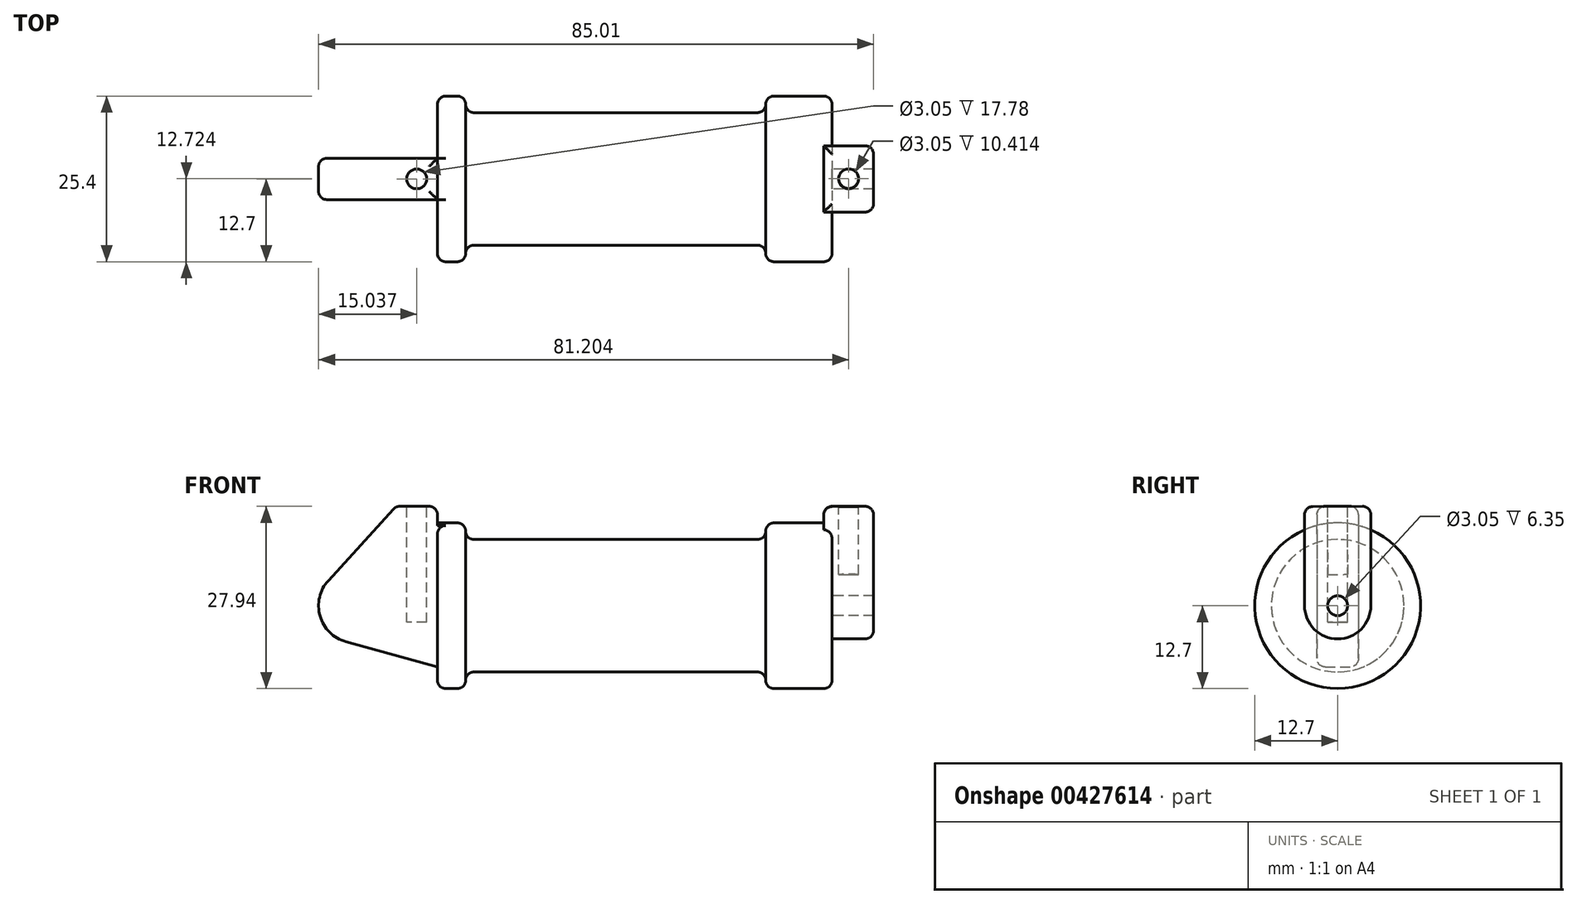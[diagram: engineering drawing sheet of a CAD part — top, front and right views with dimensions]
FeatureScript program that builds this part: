
annotation { "Feature Type Name" : "Feature", "Feature Type Description" : "" }
export const myFeature = defineFeature(function(context is Context, id is Id, definition is map)
    precondition{}
    {
        {
            var Q0;
            Q0=qCreatedBy(makeId("Front.planeOp"),FACE);
            var sketch = newSketch(context, id + "F0", { "sketchPlane" : qUnion([Q0])});
            skLineSegment(sketch, "E0", {"start": v(0, 0) * mm, "end": v(0, 12.7) * mm});
            skLineSegment(sketch, "E1", {"start": v(0, 12.7) * mm, "end": v(10.16, 12.7) * mm});
            skLineSegment(sketch, "E2", {"start": v(10.16, 12.7) * mm, "end": v(10.16, 10.16) * mm});
            skLineSegment(sketch, "E3", {"start": v(10.16, 10.16) * mm, "end": v(56.13, 10.16) * mm});
            skLineSegment(sketch, "E4", {"start": v(56.13, 10.16) * mm, "end": v(56.13, 12.7) * mm});
            skLineSegment(sketch, "E5", {"start": v(56.13, 12.7) * mm, "end": v(66.3, 12.7) * mm});
            skLineSegment(sketch, "E6", {"start": v(66.3, 12.7) * mm, "end": v(66.3, 0) * mm});
            skLineSegment(sketch, "E7", {"start": v(66.3, 0) * mm, "end": v(0, 0) * mm});
            skLineSegment(sketch, "E8", {"start": v(5.84, 15.24) * mm, "end": v(-0.5, 15.24) * mm});
            skLineSegment(sketch, "E9", {"start": v(-0.5, 15.24) * mm, "end": v(-10.88, 3.85) * mm});
            skLineSegment(sketch, "E10", {"start": v(0, 0) * mm, "end": v(-6.65, 0) * mm});
            skCircle(sketch, "E11", {"center": v(-6.65, 0) * mm, "radius": 5.72 * mm});
            skCircle(sketch, "E12", {"center": v(-6.65, 0) * mm, "radius": 3.18 * mm});
            skLineSegment(sketch, "E13", {"start": v(5.84, 15.24) * mm, "end": v(5.84, -9.4) * mm});
            skLineSegment(sketch, "E14", {"start": v(5.84, -9.4) * mm, "end": v(-8.18, -5.5) * mm});
            skSolve(sketch);
        }
        {
            var Q0;
            {var subQ0=sQuery(id+"F0.wireOp",EDGE,"E2");Q0=makeQuery(id+"F0.imprint","IMPRINT",FACE,{"disambiguationData":[TD([[makeQuery(id+"F0.imprint","IMPRINT",EDGE,{"derivedFrom":subQ0}),-1.0]])]});}
            var Q1;
            Q1=sQuery(id+"F0.wireOp",EDGE,"E7");
            revolve(context, id + "F1", {"entities" : qUnion([Q0]), "axis" : qUnion([Q1]), "revolveType" : RevolveType.FULL});
        }
        {
            var Q0;
            {var subQ1=sQuery(id+"F0.wireOp",EDGE,"E0");Q0=makeQuery(id+"F0.imprint","IMPRINT",FACE,{"disambiguationData":[TD([[makeQuery(id+"F0.imprint","IMPRINT",EDGE,{"derivedFrom":subQ1}),1.0]])]});}
            var Q1;
            {var subQ0=sQuery(id+"F0.wireOp",EDGE,"E0");Q1=makeQuery(id+"F0.imprint","IMPRINT",FACE,{"disambiguationData":[TD([[makeQuery(id+"F0.imprint","IMPRINT",EDGE,{"derivedFrom":subQ0}),-1.0]])]});}
            var Q2;
            {var subQ0=sQuery(id+"F0.wireOp",EDGE,"E12");Q2=makeQuery(id+"F0.imprint","IMPRINT",FACE,{"disambiguationData":[TD([[makeQuery(id+"F0.imprint","IMPRINT",EDGE,{"derivedFrom":subQ0}),1.0]])]});}
            var Q3;
            {var subQ0=sQuery(id+"F0.wireOp",EDGE,"E14");Q3=makeQuery(id+"F0.imprint","IMPRINT",FACE,{"disambiguationData":[TD([[makeQuery(id+"F0.imprint","IMPRINT",EDGE,{"derivedFrom":subQ0}),-1.0]])]});}
            var Q4;
            {var subQ5=sQuery(id+"F0.wireOp",EDGE,"E12");Q4=makeQuery(id+"F0.imprint","IMPRINT",FACE,{"disambiguationData":[TD([[makeQuery(id+"F0.imprint","IMPRINT",EDGE,{"derivedFrom":subQ5}),-1.0]])]});}
            extrude(context, id + "F2", {"entities" : qUnion([Q0, Q1, Q2, Q3, Q4]), "operationType" : NewBodyOperationType.ADD, "endBound" : BoundingType.SYMMETRIC, "depth" : 6.35 * mm});
        }
        {
            var Q0;
            Q0=makeQuery(id+"F1.opRevolve","SWEPT_FACE",FACE,{"disambiguationData":[OSD([sQuery(id+"F0.wireOp",EDGE,"E6")])]});
            var sketch = newSketch(context, id + "F3", { "sketchPlane" : qUnion([Q0])});
            skCircle(sketch, "E15", {"center": v(0, 0) * mm, "radius": 5.08 * mm});
            skCircle(sketch, "E16", {"center": v(0, 0) * mm, "radius": 1.52 * mm});
            skLineSegment(sketch, "E17", {"start": v(-5.08, 0) * mm, "end": v(-5.08, 15.2) * mm});
            skLineSegment(sketch, "E18", {"start": v(5.08, 0) * mm, "end": v(5.08, 15.24) * mm});
            skLineSegment(sketch, "E19", {"start": v(-5.08, 15.2) * mm, "end": v(5.08, 15.24) * mm});
            skSolve(sketch);
        }
        {
            var Q0;
            Q0=makeQuery(id+"F3.imprint","IMPRINT",FACE,{"disambiguationData":[TD([[makeQuery(id+"F3.imprint","IMPRINT",EDGE,{"derivedFrom":sQuery(id+"F3.wireOp",EDGE,"E16")}),-1.0]])]});
            var Q1;
            {var subQ0=sQuery(id+"F3.wireOp",EDGE,"E17");var subQ1=sQuery(id+"F3.wireOp",EDGE,"E15");var subQ2=makeQuery(id+"F3.imprint","INTERSECT",VERTEX,{"derivedFrom":[subQ1,subQ0]});Q1=makeQuery(id+"F3.imprint","IMPRINT",FACE,{"disambiguationData":[TD([[makeQuery(id+"F3.imprint","IMPRINT",EDGE,{"disambiguationData":[TD([[subQ2,1.0]])],"derivedFrom":subQ1}),-1.0]])]});}
            var Q2;
            {var subQ0=sQuery(id+"F3.wireOp",EDGE,"E19");Q2=makeQuery(id+"F3.imprint","IMPRINT",FACE,{"disambiguationData":[TD([[makeQuery(id+"F3.imprint","IMPRINT",EDGE,{"derivedFrom":subQ0}),-1.0]])]});}
            extrude(context, id + "F4", {"entities" : qUnion([Q0, Q1, Q2]), "operationType" : NewBodyOperationType.ADD, "depth" : 6.35 * mm});
        }
        {
            var Q0;
            Q0 = qSketchRegion(id + "F3", true);
            extrude(context, id + "F5", {"entities" : qUnion([Q0]), "operationType" : NewBodyOperationType.ADD, "oppositeDirection" : true, "depth" : 1.27 * mm});
        }
        {
            var Q0;
            Q0=makeQuery(id+"F2.opExtrude","SWEPT_FACE",FACE,{"disambiguationData":[OSD([sQuery(id+"F0.wireOp",EDGE,"E8")])]});
            var sketch = newSketch(context, id + "F6", { "sketchPlane" : qUnion([Q0])});
            skCircle(sketch, "E20", {"center": v(2.67, 0) * mm, "radius": 1.52 * mm});
            skPoint(sketch, "E20.centerSnap0", {"position": v(5.84, 0) * mm});
            skPoint(sketch, "E20.centerSnap1", {"position": v(2.67, 3.18) * mm});
            skSolve(sketch);
        }
        {
            var Q0;
            Q0=makeQuery(id+"F6.imprint","IMPRINT",FACE,{"disambiguationData":[TD([[makeQuery(id+"F6.imprint","IMPRINT",EDGE,{"derivedFrom":sQuery(id+"F6.wireOp",EDGE,"E20")}),1.0]])]});
            extrude(context, id + "F7", {"entities" : qUnion([Q0]), "operationType" : NewBodyOperationType.REMOVE, "oppositeDirection" : true, "depth" : 17.78 * mm});
        }
        {
            var Q0;
            {var subQ0=sQuery(id+"F3.wireOp",EDGE,"E19");Q0=makeQuery(id+"F5.boolean.opBoolean","MERGE",FACE,{"derivedFrom":[makeQuery(id+"F4.opExtrude","SWEPT_FACE",FACE,{"disambiguationData":[OSD([subQ0])]}),makeQuery(id+"F5.opExtrude","SWEPT_FACE",FACE,{"disambiguationData":[OSD([subQ0])]})]});}
            var sketch = newSketch(context, id + "F8", { "sketchPlane" : qUnion([Q0])});
            skCircle(sketch, "E21", {"center": v(68.83, 0.07) * mm, "radius": 1.52 * mm});
            skPoint(sketch, "E21.centerSnap0", {"position": v(72.64, 0.07) * mm});
            skPoint(sketch, "E21.centerSnap1", {"position": v(68.83, 5.15) * mm});
            skSolve(sketch);
        }
        {
            var Q0;
            Q0=makeQuery(id+"F8.imprint","IMPRINT",FACE,{"disambiguationData":[TD([[makeQuery(id+"F8.imprint","IMPRINT",EDGE,{"derivedFrom":sQuery(id+"F8.wireOp",EDGE,"E21")}),1.0]])]});
            extrude(context, id + "F9", {"entities" : qUnion([Q0]), "operationType" : NewBodyOperationType.REMOVE, "oppositeDirection" : true, "depth" : 10.4 * mm});
        }
        {
            var Q0;
            Q0=makeQuery(id+"F1.opRevolve","SWEPT_EDGE",EDGE,{"disambiguationData":[OSD([sQuery(id+"F0.wireOp",EDGE,"E1"),sQuery(id+"F0.wireOp",EDGE,"E2")])]});
            var Q1;
            Q1=makeQuery(id+"F1.opRevolve","SWEPT_EDGE",EDGE,{"disambiguationData":[OSD([sQuery(id+"F0.wireOp",EDGE,"E2"),sQuery(id+"F0.wireOp",EDGE,"E3")])]});
            var Q2;
            Q2=makeQuery(id+"F1.opRevolve","SWEPT_EDGE",EDGE,{"disambiguationData":[OSD([sQuery(id+"F0.wireOp",EDGE,"E4"),sQuery(id+"F0.wireOp",EDGE,"E5")])]});
            var Q3;
            Q3=makeQuery(id+"F1.opRevolve","SWEPT_EDGE",EDGE,{"disambiguationData":[OSD([sQuery(id+"F0.wireOp",EDGE,"E3"),sQuery(id+"F0.wireOp",EDGE,"E4")])]});
            var Q4;
            {var subQ0=sQuery(id+"F0.wireOp",EDGE,"E1");var subQ1=sQuery(id+"F0.wireOp",EDGE,"E13");Q4=makeQuery(id+"F2.boolean.opBoolean","SPLIT",EDGE,{"disambiguationData":[topologyDisambiguationEdgeConnected([makeQuery(id+"F1.opRevolve","SWEPT_FACE",FACE,{"disambiguationData":[OSD([subQ1])]})])],"derivedFrom":makeQuery(id+"F1.opRevolve","SWEPT_EDGE",EDGE,{"disambiguationData":[OSD([subQ0,subQ1])]})});}
            var Q5;
            Q5=makeQuery(id+"F2.opExtrude","SWEPT_EDGE",EDGE,{"disambiguationData":[OSD([sQuery(id+"F0.wireOp",EDGE,"E8"),sQuery(id+"F0.wireOp",EDGE,"E13")])]});
            var Q6;
            Q6=makeQuery(id+"F2.opExtrude","CAP_EDGE",EDGE,{"disambiguationData":[OSD([sQuery(id+"F0.wireOp",EDGE,"E8")])],"isStart":false});
            var Q7;
            Q7=makeQuery(id+"F2.opExtrude","CAP_EDGE",EDGE,{"disambiguationData":[OSD([sQuery(id+"F0.wireOp",EDGE,"E8")])],"isStart":true});
            var Q8;
            Q8=makeQuery(id+"F2.opExtrude","SWEPT_EDGE",EDGE,{"disambiguationData":[OSD([sQuery(id+"F0.wireOp",EDGE,"E8"),sQuery(id+"F0.wireOp",EDGE,"E9")])]});
            var Q9;
            Q9=makeQuery(id+"F2.opExtrude","CAP_EDGE",EDGE,{"disambiguationData":[OSD([sQuery(id+"F0.wireOp",EDGE,"E9")])],"isStart":false});
            var Q10;
            Q10=makeQuery(id+"F2.opExtrude","CAP_EDGE",EDGE,{"disambiguationData":[OSD([sQuery(id+"F0.wireOp",EDGE,"E9")])],"isStart":true});
            var Q11;
            {var subQ0=sQuery(id+"F0.wireOp",EDGE,"E5");var subQ1=sQuery(id+"F0.wireOp",EDGE,"E6");Q11=makeQuery(id+"F4.boolean.opBoolean","SPLIT",EDGE,{"disambiguationData":[topologyDisambiguationEdgeConnected([makeQuery(id+"F1.opRevolve","SWEPT_FACE",FACE,{"disambiguationData":[OSD([subQ1])]})])],"derivedFrom":makeQuery(id+"F1.opRevolve","SWEPT_EDGE",EDGE,{"disambiguationData":[OSD([subQ0,subQ1])]})});}
            var Q12;
            Q12=makeQuery(id+"F5.opExtrude","CAP_EDGE",EDGE,{"disambiguationData":[OSD([sQuery(id+"F3.wireOp",EDGE,"E19")])],"isStart":false});
            var Q13;
            {var subQ0=sQuery(id+"F3.wireOp",EDGE,"E19");var subQ1=sQuery(id+"F3.wireOp",EDGE,"E18");Q13=makeQuery(id+"F5.boolean.opBoolean","MERGE",EDGE,{"derivedFrom":[makeQuery(id+"F4.opExtrude","SWEPT_EDGE",EDGE,{"disambiguationData":[OSD([subQ1,subQ0])]}),makeQuery(id+"F5.opExtrude","SWEPT_EDGE",EDGE,{"disambiguationData":[OSD([subQ1,subQ0])]})]});}
            var Q14;
            Q14=makeQuery(id+"F4.opExtrude","CAP_EDGE",EDGE,{"disambiguationData":[OSD([sQuery(id+"F3.wireOp",EDGE,"E19")])],"isStart":false});
            var Q15;
            {var subQ0=sQuery(id+"F3.wireOp",EDGE,"E19");var subQ1=sQuery(id+"F3.wireOp",EDGE,"E17");Q15=makeQuery(id+"F5.boolean.opBoolean","MERGE",EDGE,{"derivedFrom":[makeQuery(id+"F4.opExtrude","SWEPT_EDGE",EDGE,{"disambiguationData":[OSD([subQ1,subQ0])]}),makeQuery(id+"F5.opExtrude","SWEPT_EDGE",EDGE,{"disambiguationData":[OSD([subQ1,subQ0])]})]});}
            var Q16;
            {var subQ0=sQuery(id+"F3.wireOp",EDGE,"E18");Q16=makeQuery(id+"F4.boolean.opBoolean","SPLIT",EDGE,{"disambiguationData":[topologyDisambiguationEdgeConnected([makeQuery(id+"F1.opRevolve","SWEPT_FACE",FACE,{"disambiguationData":[OSD([sQuery(id+"F0.wireOp",EDGE,"E6")])]})])],"derivedFrom":makeQuery(id+"F4.opExtrude","CAP_EDGE",EDGE,{"disambiguationData":[OSD([subQ0])],"isStart":true})});}
            var Q17;
            Q17=makeQuery(id+"F4.opExtrude","CAP_EDGE",EDGE,{"disambiguationData":[OSD([sQuery(id+"F3.wireOp",EDGE,"E18")])],"isStart":false});
            fillet(context, id + "F10", {"entities" : qUnion([Q0, Q1, Q2, Q3, Q4, Q5, Q6, Q7, Q8, Q9, Q10, Q11, Q12, Q13, Q14, Q15, Q16, Q17]), "radius" : 1.27 * mm, "tangentPropagation" : true, "allowEdgeOverflow" : false});
        }
    });
